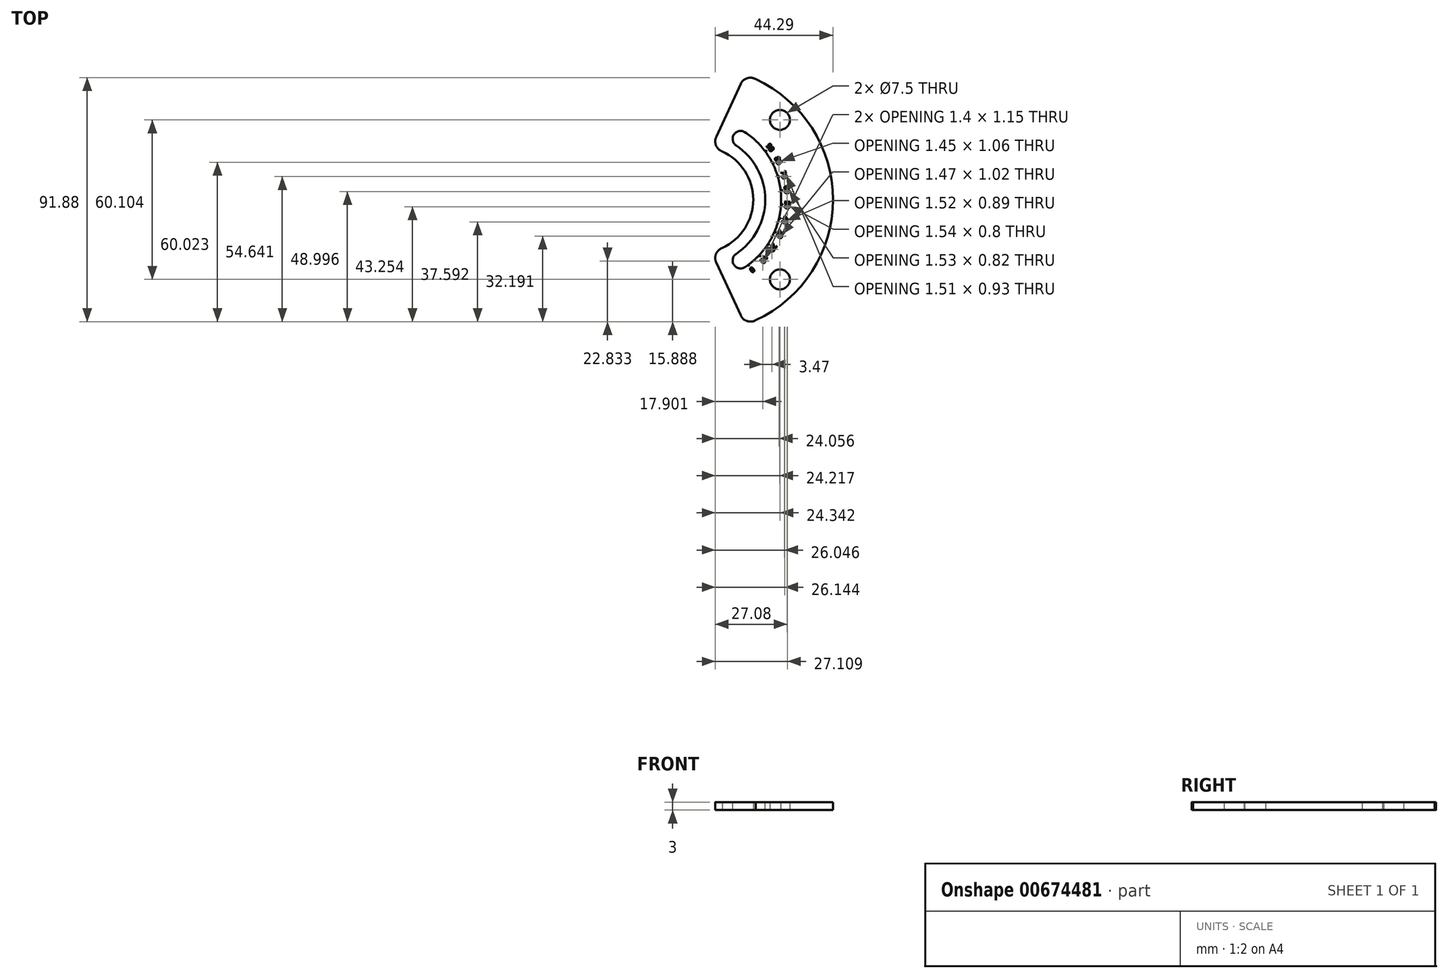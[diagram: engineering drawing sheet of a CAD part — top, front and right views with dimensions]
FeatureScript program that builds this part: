
annotation { "Feature Type Name" : "Feature", "Feature Type Description" : "" }
export const myFeature = defineFeature(function(context is Context, id is Id, definition is map)
    precondition{}
    {
        {
            var Q0;
            Q0=qCreatedBy(makeId("Top.planeOp"),FACE);
            var sketch = newSketch(context, id + "F0", { "sketchPlane" : qUnion([Q0])});
            skCircle(sketch, "E0", {"center": v(0, 0) * mm, "radius": 42.5 * mm, "construction": true});
            skLineSegment(sketch, "E1", {"start": v(0, 0) * mm, "end": v(30.05, 30.05) * mm, "construction": true});
            skCircle(sketch, "E2", {"center": v(30.05, 30.05) * mm, "radius": 3.75 * mm});
            skCircle(sketch, "E3.1.0", {"center": v(-30.05, 30.05) * mm, "radius": 3.75 * mm});
            skCircle(sketch, "E3.2.0", {"center": v(-30.05, -30.05) * mm, "radius": 3.75 * mm});
            skCircle(sketch, "E3.3.0", {"center": v(30.05, -30.05) * mm, "radius": 3.75 * mm});
            skLineSegment(sketch, "E4", {"start": v(0, 0) * mm, "end": v(30.05, -30.05) * mm, "construction": true});
            skSolve(sketch);
        }
        {
            var Q0;
            Q0=qCreatedBy(makeId("Top.planeOp"),FACE);
            var sketch = newSketch(context, id + "F1", { "sketchPlane" : qUnion([Q0])});
            skLineSegment(sketch, "E5", {"start": v(6.08, 23.6) * mm, "end": v(15.3, 43.61) * mm});
            skLineSegment(sketch, "E6", {"start": v(6.08, -23.6) * mm, "end": v(15.3, -43.61) * mm});
            skLineSegment(sketch, "E7", {"start": v(0, 0) * mm, "end": v(0, 47.02) * mm, "construction": true});
            skLineSegment(sketch, "E8", {"start": v(0, 0) * mm, "end": v(0, -46.33) * mm, "construction": true});
            skPoint(sketch, "E9.visualSharp", {"position": v(16.58, 46.4) * mm});
            skArc(sketch, "E9.filletArc", {"start": v(20.9, 45.42) * mm, "mid": v(17.7, 45.75) * mm, "end": v(15.3, 43.61) * mm});
            skPoint(sketch, "E10.visualSharp", {"position": v(3.88, 18.83) * mm});
            skArc(sketch, "E10.filletArc", {"start": v(6.08, 23.6) * mm, "mid": v(6.02, 20.4) * mm, "end": v(8.35, 18.17) * mm});
            skPoint(sketch, "E11.visualSharp", {"position": v(3.88, -18.83) * mm});
            skArc(sketch, "E11.filletArc", {"start": v(8.35, -18.17) * mm, "mid": v(6.02, -20.4) * mm, "end": v(6.08, -23.6) * mm});
            skPoint(sketch, "E12.visualSharp", {"position": v(16.58, -46.4) * mm});
            skArc(sketch, "E12.filletArc", {"start": v(15.3, -43.61) * mm, "mid": v(17.7, -45.75) * mm, "end": v(20.9, -45.42) * mm});
            skLineSegment(sketch, "E13", {"start": v(0, 0) * mm, "end": v(50, 0) * mm, "construction": true});
            skArc(sketch, "E14", {"start": v(8.35, 18.17) * mm, "mid": v(20, 0) * mm, "end": v(8.35, -18.17) * mm});
            skArc(sketch, "E15", {"start": v(20.9, 45.42) * mm, "mid": v(50, 0) * mm, "end": v(20.9, -45.42) * mm});
            skLineSegment(sketch, "E16", {"start": v(20.9, 45.42) * mm, "end": v(20.9, 0) * mm, "construction": true});
            skLineSegment(sketch, "E17", {"start": v(20.9, 0) * mm, "end": v(20.9, -45.42) * mm, "construction": true});
            skLineSegment(sketch, "E18", {"start": v(0, 43.61) * mm, "end": v(15.3, 43.61) * mm, "construction": true});
            skLineSegment(sketch, "E19", {"start": v(0, -43.61) * mm, "end": v(15.3, -43.61) * mm, "construction": true});
            skSolve(sketch);
        }
        {
            var Q0;
            Q0=makeQuery(id+"F1.imprint","IMPRINT",FACE,{"disambiguationData":[TD([[makeQuery(id+"F1.imprint","IMPRINT",EDGE,{"derivedFrom":sQuery(id+"F1.wireOp",EDGE,"E5")}),-1.0]])]});
            extrude(context, id + "F2", {"entities" : qUnion([Q0]), "depth" : 3 * mm, "offsetDistance" : 25 * mm});
        }
        {
            var Q0;
            Q0=makeQuery(id+"F0.imprint","IMPRINT",FACE,{"disambiguationData":[TD([[makeQuery(id+"F0.imprint","IMPRINT",EDGE,{"derivedFrom":sQuery(id+"F0.wireOp",EDGE,"E2")}),1.0]])]});
            var Q1;
            Q1=makeQuery(id+"F0.imprint","IMPRINT",FACE,{"disambiguationData":[TD([[makeQuery(id+"F0.imprint","IMPRINT",EDGE,{"derivedFrom":sQuery(id+"F0.wireOp",EDGE,"E3.3.0")}),1.0]])]});
            extrude(context, id + "F3", {"entities" : qUnion([Q0, Q1]), "operationType" : NewBodyOperationType.REMOVE, "depth" : 25 * mm, "offsetDistance" : 25 * mm});
        }
        {
            var Q0;
            Q0=makeQuery(id+"F2.opExtrude","CAP_FACE",FACE,{"disambiguationData":[OSD([sQuery(id+"F1.wireOp",EDGE,"KiuFZQME-wWnU-ktu5-Gd9x-qji5TMNZz2fd"),sQuery(id+"F1.wireOp",EDGE,"G5eraXv0-ftC7-V2Hx-4i3N-1R2XA50WnSdq"),sQuery(id+"F1.wireOp",EDGE,"E5"),sQuery(id+"F1.wireOp",EDGE,"E6"),sQuery(id+"F1.wireOp",EDGE,"57560024-62e8-479f-91f4-8b403f4d0ad7.filletArc"),sQuery(id+"F1.wireOp",EDGE,"ddf71622-e854-4fa8-aca5-087326283111.filletArc"),sQuery(id+"F1.wireOp",EDGE,"85b82a5b-4425-4996-801d-5779b438c59f.filletArc"),sQuery(id+"F1.wireOp",EDGE,"35c327b1-5974-4460-b54d-dc77ba413df5.filletArc")])],"isStart":false});
            var sketch = newSketch(context, id + "F4", { "sketchPlane" : qUnion([Q0])});
            skArc(sketch, "E20", {"start": v(13.6, 20.4) * mm, "mid": v(24.52, 0) * mm, "end": v(13.6, -20.4) * mm});
            skArc(sketch, "E21", {"start": v(16.92, 25.4) * mm, "mid": v(30.52, 0) * mm, "end": v(16.92, -25.4) * mm});
            skLineSegment(sketch, "E22", {"start": v(0, 0) * mm, "end": v(16.92, -25.4) * mm, "construction": true});
            skLineSegment(sketch, "E23", {"start": v(0, 0) * mm, "end": v(16.92, 25.4) * mm, "construction": true});
            skLineSegment(sketch, "E24", {"start": v(13.6, 20.4) * mm, "end": v(13.6, 0) * mm, "construction": true});
            skLineSegment(sketch, "E25", {"start": v(13.6, 0) * mm, "end": v(13.6, -20.4) * mm, "construction": true});
            skArc(sketch, "E26", {"start": v(13.6, 20.4) * mm, "mid": v(12.76, 24.57) * mm, "end": v(16.92, 25.4) * mm});
            skArc(sketch, "E27", {"start": v(13.6, -20.4) * mm, "mid": v(12.76, -24.57) * mm, "end": v(16.92, -25.4) * mm});
            skSolve(sketch);
        }
        {
            var Q0;
            Q0=qSketchRegion(id+"F4",true);
            extrude(context, id + "F5", {"entities" : qUnion([Q0]), "operationType" : NewBodyOperationType.REMOVE, "oppositeDirection" : true, "depth" : 25 * mm, "offsetDistance" : 25 * mm});
        }
        {
            var Q0;
            Q0=makeQuery(id+"F2.opExtrude","CAP_FACE",FACE,{"disambiguationData":[OSD([sQuery(id+"F1.wireOp",EDGE,"E5"),sQuery(id+"F1.wireOp",EDGE,"E6"),sQuery(id+"F1.wireOp",EDGE,"E9.filletArc"),sQuery(id+"F1.wireOp",EDGE,"E10.filletArc"),sQuery(id+"F1.wireOp",EDGE,"E11.filletArc"),sQuery(id+"F1.wireOp",EDGE,"E12.filletArc"),sQuery(id+"F1.wireOp",EDGE,"E14"),sQuery(id+"F1.wireOp",EDGE,"E15")])],"isStart":false});
            var sketch = newSketch(context, id + "F6", { "sketchPlane" : qUnion([Q0])});
            skLineSegment(sketch, "E28", {"start": v(0, 39.25) * mm, "end": v(0, -36.96) * mm, "construction": true});
            skPoint(sketch, "E29.center", {"position": v(0, 0) * mm});
            skLineSegment(sketch, "E30.1.0", {"start": v(21.84, -20.36) * mm, "end": v(21.67, -20.54) * mm});
            skLineSegment(sketch, "E30.1.1", {"start": v(22.8, -21.26) * mm, "end": v(21.84, -20.36) * mm});
            skLineSegment(sketch, "E30.1.2", {"start": v(21.67, -20.54) * mm, "end": v(22.63, -21.44) * mm});
            skLineSegment(sketch, "E30.1.3", {"start": v(22.63, -21.44) * mm, "end": v(22.8, -21.26) * mm});
            skLineSegment(sketch, "E30.2.0", {"start": v(25.04, -16.27) * mm, "end": v(24.9, -16.48) * mm});
            skLineSegment(sketch, "E30.2.1", {"start": v(26.14, -16.99) * mm, "end": v(25.04, -16.27) * mm});
            skLineSegment(sketch, "E30.2.2", {"start": v(24.9, -16.48) * mm, "end": v(26, -17.2) * mm});
            skLineSegment(sketch, "E30.2.3", {"start": v(26, -17.2) * mm, "end": v(26.14, -16.99) * mm});
            skLineSegment(sketch, "E30.3.0", {"start": v(27.48, -11.68) * mm, "end": v(27.38, -11.91) * mm});
            skLineSegment(sketch, "E30.3.1", {"start": v(28.69, -12.2) * mm, "end": v(27.48, -11.68) * mm});
            skLineSegment(sketch, "E30.3.2", {"start": v(27.38, -11.91) * mm, "end": v(28.59, -12.43) * mm});
            skLineSegment(sketch, "E30.3.3", {"start": v(28.59, -12.43) * mm, "end": v(28.69, -12.2) * mm});
            skLineSegment(sketch, "E30.4.0", {"start": v(29.09, -6.75) * mm, "end": v(29.03, -7) * mm});
            skLineSegment(sketch, "E30.4.1", {"start": v(30.37, -7.05) * mm, "end": v(29.09, -6.75) * mm});
            skLineSegment(sketch, "E30.4.2", {"start": v(29.03, -7) * mm, "end": v(30.31, -7.3) * mm});
            skLineSegment(sketch, "E30.4.3", {"start": v(30.31, -7.3) * mm, "end": v(30.37, -7.05) * mm});
            skLineSegment(sketch, "E30.5.0", {"start": v(29.81, -1.6) * mm, "end": v(29.8, -1.86) * mm});
            skLineSegment(sketch, "E30.5.1", {"start": v(31.13, -1.69) * mm, "end": v(29.81, -1.6) * mm});
            skLineSegment(sketch, "E30.5.2", {"start": v(29.8, -1.86) * mm, "end": v(31.12, -1.94) * mm});
            skLineSegment(sketch, "E30.5.3", {"start": v(31.12, -1.94) * mm, "end": v(31.13, -1.69) * mm});
            skLineSegment(sketch, "E30.6.0", {"start": v(29.64, 3.58) * mm, "end": v(29.67, 3.33) * mm});
            skLineSegment(sketch, "E30.6.1", {"start": v(30.95, 3.73) * mm, "end": v(29.64, 3.58) * mm});
            skLineSegment(sketch, "E30.6.2", {"start": v(29.67, 3.33) * mm, "end": v(30.98, 3.48) * mm});
            skLineSegment(sketch, "E30.6.3", {"start": v(30.98, 3.48) * mm, "end": v(30.95, 3.73) * mm});
            skLineSegment(sketch, "E30.7.0", {"start": v(28.58, 8.66) * mm, "end": v(28.65, 8.42) * mm});
            skLineSegment(sketch, "E30.7.1", {"start": v(29.84, 9.04) * mm, "end": v(28.58, 8.66) * mm});
            skLineSegment(sketch, "E30.7.2", {"start": v(28.65, 8.42) * mm, "end": v(29.9, 8.8) * mm});
            skLineSegment(sketch, "E30.7.3", {"start": v(29.9, 8.8) * mm, "end": v(29.84, 9.04) * mm});
            skLineSegment(sketch, "E30.8.0", {"start": v(26.64, 13.48) * mm, "end": v(26.76, 13.25) * mm});
            skLineSegment(sketch, "E30.8.1", {"start": v(27.82, 14.07) * mm, "end": v(26.64, 13.48) * mm});
            skLineSegment(sketch, "E30.8.2", {"start": v(26.76, 13.25) * mm, "end": v(27.93, 13.84) * mm});
            skLineSegment(sketch, "E30.8.3", {"start": v(27.93, 13.84) * mm, "end": v(27.82, 14.07) * mm});
            skLineSegment(sketch, "E30.anchor1", {"start": v(0, 0) * mm, "end": v(17.79, -23.98) * mm, "construction": true});
            skLineSegment(sketch, "E31.2.9.0", {"start": v(23.9, 17.89) * mm, "end": v(24.06, 17.69) * mm});
            skLineSegment(sketch, "E31.3.9.0", {"start": v(24.97, 18.67) * mm, "end": v(23.9, 17.89) * mm});
            skLineSegment(sketch, "E31.6.9.0", {"start": v(24.06, 17.69) * mm, "end": v(25.11, 18.47) * mm});
            skLineSegment(sketch, "E31.9.9.0", {"start": v(25.11, 18.47) * mm, "end": v(24.97, 18.67) * mm});
            skLineSegment(sketch, "E32", {"start": v(0, 0) * mm, "end": v(24.51, 18.18) * mm, "construction": true});
            skLineSegment(sketch, "E33", {"start": v(17.79, -23.98) * mm, "end": v(17.69, -24.06) * mm});
            skLineSegment(sketch, "E34", {"start": v(17.69, -24.06) * mm, "end": v(18.38, -24.99) * mm});
            skLineSegment(sketch, "E35", {"start": v(18.38, -24.99) * mm, "end": v(18.58, -24.84) * mm});
            skLineSegment(sketch, "E36", {"start": v(18.58, -24.84) * mm, "end": v(17.89, -23.9) * mm});
            skLineSegment(sketch, "E37", {"start": v(17.89, -23.9) * mm, "end": v(17.79, -23.98) * mm});
            skLineSegment(sketch, "E38.1.0", {"start": v(0, 0) * mm, "end": v(21.68, -20.53) * mm, "construction": true});
            skLineSegment(sketch, "E38.2.0", {"start": v(0, 0) * mm, "end": v(24.92, -16.45) * mm, "construction": true});
            skLineSegment(sketch, "E38.3.0", {"start": v(0, 0) * mm, "end": v(27.4, -11.88) * mm, "construction": true});
            skLineSegment(sketch, "E38.4.0", {"start": v(0, 0) * mm, "end": v(29.04, -6.94) * mm, "construction": true});
            skLineSegment(sketch, "E38.5.0", {"start": v(0, 0) * mm, "end": v(29.8, -1.8) * mm, "construction": true});
            skLineSegment(sketch, "E38.6.0", {"start": v(0, 0) * mm, "end": v(29.66, 3.41) * mm, "construction": true});
            skLineSegment(sketch, "E38.7.0", {"start": v(0, 0) * mm, "end": v(28.62, 8.51) * mm, "construction": true});
            skLineSegment(sketch, "E38.8.0", {"start": v(0, 0) * mm, "end": v(26.7, 13.35) * mm, "construction": true});
            skLineSegment(sketch, "E38.9.0", {"start": v(0, 0) * mm, "end": v(23.98, 17.79) * mm, "construction": true});
            skLineSegment(sketch, "E38.anchor2", {"start": v(0, 0) * mm, "end": v(23.98, 17.79) * mm, "construction": true});
            skSolve(sketch);
        }
        {
            var Q0;
            {var subQ0=sQuery(id+"F6.wireOp",EDGE,"594Twtlv-L5ni-ZomQ-KuFa-bSSoLLlrFaCu");Q0=makeQuery(id+"F6.imprint","IMPRINT",FACE,{"disambiguationData":[TD([[makeQuery(id+"F6.imprint","IMPRINT",EDGE,{"derivedFrom":subQ0}),1.0]])]});}
            var Q1;
            {var subQ0=sQuery(id+"F6.wireOp",EDGE,"YlrvQvtq-lzJw-h0mC-7lxV-1P0NOcUl3Lp0");Q1=makeQuery(id+"F6.imprint","IMPRINT",FACE,{"disambiguationData":[TD([[makeQuery(id+"F6.imprint","IMPRINT",EDGE,{"derivedFrom":subQ0}),1.0]])]});}
            var Q2;
            {var subQ0=sQuery(id+"F6.wireOp",EDGE,"E30.1.0");Q2=makeQuery(id+"F6.imprint","IMPRINT",FACE,{"disambiguationData":[TD([[makeQuery(id+"F6.imprint","IMPRINT",EDGE,{"derivedFrom":subQ0}),1.0]])]});}
            var Q3;
            {var subQ0=sQuery(id+"F6.wireOp",EDGE,"E30.1.3");Q3=makeQuery(id+"F6.imprint","IMPRINT",FACE,{"disambiguationData":[TD([[makeQuery(id+"F6.imprint","IMPRINT",EDGE,{"derivedFrom":subQ0}),1.0]])]});}
            var Q4;
            {var subQ0=sQuery(id+"F6.wireOp",EDGE,"E30.2.0");Q4=makeQuery(id+"F6.imprint","IMPRINT",FACE,{"disambiguationData":[TD([[makeQuery(id+"F6.imprint","IMPRINT",EDGE,{"derivedFrom":subQ0}),1.0]])]});}
            var Q5;
            {var subQ0=sQuery(id+"F6.wireOp",EDGE,"E30.2.3");Q5=makeQuery(id+"F6.imprint","IMPRINT",FACE,{"disambiguationData":[TD([[makeQuery(id+"F6.imprint","IMPRINT",EDGE,{"derivedFrom":subQ0}),1.0]])]});}
            var Q6;
            {var subQ0=sQuery(id+"F6.wireOp",EDGE,"E30.3.0");Q6=makeQuery(id+"F6.imprint","IMPRINT",FACE,{"disambiguationData":[TD([[makeQuery(id+"F6.imprint","IMPRINT",EDGE,{"derivedFrom":subQ0}),1.0]])]});}
            var Q7;
            {var subQ0=sQuery(id+"F6.wireOp",EDGE,"E30.3.3");Q7=makeQuery(id+"F6.imprint","IMPRINT",FACE,{"disambiguationData":[TD([[makeQuery(id+"F6.imprint","IMPRINT",EDGE,{"derivedFrom":subQ0}),1.0]])]});}
            var Q8;
            {var subQ0=sQuery(id+"F6.wireOp",EDGE,"E30.4.0");Q8=makeQuery(id+"F6.imprint","IMPRINT",FACE,{"disambiguationData":[TD([[makeQuery(id+"F6.imprint","IMPRINT",EDGE,{"derivedFrom":subQ0}),1.0]])]});}
            var Q9;
            {var subQ0=sQuery(id+"F6.wireOp",EDGE,"E30.4.3");Q9=makeQuery(id+"F6.imprint","IMPRINT",FACE,{"disambiguationData":[TD([[makeQuery(id+"F6.imprint","IMPRINT",EDGE,{"derivedFrom":subQ0}),1.0]])]});}
            var Q10;
            {var subQ0=sQuery(id+"F6.wireOp",EDGE,"E30.5.0");Q10=makeQuery(id+"F6.imprint","IMPRINT",FACE,{"disambiguationData":[TD([[makeQuery(id+"F6.imprint","IMPRINT",EDGE,{"derivedFrom":subQ0}),1.0]])]});}
            var Q11;
            {var subQ0=sQuery(id+"F6.wireOp",EDGE,"E30.6.0");Q11=makeQuery(id+"F6.imprint","IMPRINT",FACE,{"disambiguationData":[TD([[makeQuery(id+"F6.imprint","IMPRINT",EDGE,{"derivedFrom":subQ0}),1.0]])]});}
            var Q12;
            {var subQ0=sQuery(id+"F6.wireOp",EDGE,"E30.6.3");Q12=makeQuery(id+"F6.imprint","IMPRINT",FACE,{"disambiguationData":[TD([[makeQuery(id+"F6.imprint","IMPRINT",EDGE,{"derivedFrom":subQ0}),1.0]])]});}
            var Q13;
            {var subQ0=sQuery(id+"F6.wireOp",EDGE,"E30.5.3");Q13=makeQuery(id+"F6.imprint","IMPRINT",FACE,{"disambiguationData":[TD([[makeQuery(id+"F6.imprint","IMPRINT",EDGE,{"derivedFrom":subQ0}),1.0]])]});}
            var Q14;
            {var subQ0=sQuery(id+"F6.wireOp",EDGE,"E30.7.0");Q14=makeQuery(id+"F6.imprint","IMPRINT",FACE,{"disambiguationData":[TD([[makeQuery(id+"F6.imprint","IMPRINT",EDGE,{"derivedFrom":subQ0}),1.0]])]});}
            var Q15;
            {var subQ0=sQuery(id+"F6.wireOp",EDGE,"E30.7.3");Q15=makeQuery(id+"F6.imprint","IMPRINT",FACE,{"disambiguationData":[TD([[makeQuery(id+"F6.imprint","IMPRINT",EDGE,{"derivedFrom":subQ0}),1.0]])]});}
            var Q16;
            {var subQ0=sQuery(id+"F6.wireOp",EDGE,"E30.8.0");Q16=makeQuery(id+"F6.imprint","IMPRINT",FACE,{"disambiguationData":[TD([[makeQuery(id+"F6.imprint","IMPRINT",EDGE,{"derivedFrom":subQ0}),1.0]])]});}
            var Q17;
            {var subQ0=sQuery(id+"F6.wireOp",EDGE,"E30.8.3");Q17=makeQuery(id+"F6.imprint","IMPRINT",FACE,{"disambiguationData":[TD([[makeQuery(id+"F6.imprint","IMPRINT",EDGE,{"derivedFrom":subQ0}),1.0]])]});}
            var Q18;
            {var subQ0=sQuery(id+"F6.wireOp",EDGE,"E35");Q18=makeQuery(id+"F6.imprint","IMPRINT",FACE,{"disambiguationData":[TD([[makeQuery(id+"F6.imprint","IMPRINT",EDGE,{"derivedFrom":subQ0}),1.0]])]});}
            var Q19;
            {var subQ2=sQuery(id+"F6.wireOp",EDGE,"E33");Q19=makeQuery(id+"F6.imprint","IMPRINT",FACE,{"disambiguationData":[TD([[makeQuery(id+"F6.imprint","IMPRINT",EDGE,{"derivedFrom":subQ2}),1.0]])]});}
            var Q20;
            {var subQ0=sQuery(id+"F6.wireOp",EDGE,"E31.9.9.0");Q20=makeQuery(id+"F6.imprint","IMPRINT",FACE,{"disambiguationData":[TD([[makeQuery(id+"F6.imprint","IMPRINT",EDGE,{"derivedFrom":subQ0}),1.0]])]});}
            var Q21;
            {var subQ0=sQuery(id+"F6.wireOp",EDGE,"E31.2.9.0");Q21=makeQuery(id+"F6.imprint","IMPRINT",FACE,{"disambiguationData":[TD([[makeQuery(id+"F6.imprint","IMPRINT",EDGE,{"derivedFrom":subQ0}),1.0]])]});}
            extrude(context, id + "F7", {"entities" : qUnion([Q0, Q1, Q2, Q3, Q4, Q5, Q6, Q7, Q8, Q9, Q10, Q11, Q12, Q13, Q14, Q15, Q16, Q17, Q18, Q19, Q20, Q21]), "operationType" : NewBodyOperationType.REMOVE, "oppositeDirection" : true, "depth" : 0.1 * mm, "offsetDistance" : 25 * mm});
        }
        {
            var Q0;
            Q0=makeQuery(id+"F2.opExtrude","CAP_FACE",FACE,{"disambiguationData":[OSD([sQuery(id+"F1.wireOp",EDGE,"E5"),sQuery(id+"F1.wireOp",EDGE,"E6"),sQuery(id+"F1.wireOp",EDGE,"E9.filletArc"),sQuery(id+"F1.wireOp",EDGE,"E10.filletArc"),sQuery(id+"F1.wireOp",EDGE,"E11.filletArc"),sQuery(id+"F1.wireOp",EDGE,"E12.filletArc"),sQuery(id+"F1.wireOp",EDGE,"E14"),sQuery(id+"F1.wireOp",EDGE,"E15")])],"isStart":false});
            var sketch = newSketch(context, id + "F8", { "sketchPlane" : qUnion([Q0])});
            skText(sketch, "E39", { "text": "10", "fontName": "OpenSans-Regular.ttf"});
            skText(sketch, "E40", { "text": "20", "fontName": "OpenSans-Regular.ttf"});
            skPoint(sketch, "E41", {"position": v(26.88, -14.45) * mm});
            skText(sketch, "E42", { "text": "30", "fontName": "OpenSans-Regular.ttf"});
            skText(sketch, "E43", { "text": "40\n", "fontName": "OpenSans-Regular.ttf"});
            skText(sketch, "E44", { "text": "50", "fontName": "OpenSans-Regular.ttf"});
            skText(sketch, "E45", { "text": "60", "fontName": "OpenSans-Regular.ttf"});
            skText(sketch, "E46", { "text": "70", "fontName": "OpenSans-Regular.ttf"});
            skText(sketch, "E47", { "text": "80", "fontName": "OpenSans-Regular.ttf"});
            skText(sketch, "E48", { "text": "90", "fontName": "OpenSans-Regular.ttf"});
            skText(sketch, "E49", { "text": "0", "fontName": "OpenSans-Regular.ttf"});
            skLineSegment(sketch, "E50", {"start": v(0, 0) * mm, "end": v(19.06, -25.7) * mm, "construction": true});
            skLineSegment(sketch, "E51", {"start": v(0, 0) * mm, "end": v(23.24, -22) * mm, "construction": true});
            skLineSegment(sketch, "E52", {"start": v(0, 0) * mm, "end": v(26.7, -17.63) * mm, "construction": true});
            skLineSegment(sketch, "E53", {"start": v(0, 0) * mm, "end": v(29.36, -12.73) * mm, "construction": true});
            skLineSegment(sketch, "E54", {"start": v(0, 0) * mm, "end": v(31.12, -7.44) * mm, "construction": true});
            skLineSegment(sketch, "E55", {"start": v(0, 0) * mm, "end": v(31.94, -1.92) * mm, "construction": true});
            skLineSegment(sketch, "E56", {"start": v(0, 0) * mm, "end": v(31.8, 3.66) * mm, "construction": true});
            skPoint(sketch, "E56.endSnap0", {"position": v(31.8, 3.66) * mm});
            skLineSegment(sketch, "E57", {"start": v(0, 0) * mm, "end": v(30.67, 9.12) * mm, "construction": true});
            skLineSegment(sketch, "E58", {"start": v(0, 0) * mm, "end": v(28.62, 14.3) * mm, "construction": true});
            skLineSegment(sketch, "E59", {"start": v(0, 0) * mm, "end": v(25.7, 19.06) * mm, "construction": true});
            const initialGuessF8  = {"E39": [0.02406, -0.02075, -0.55104, -0.83448, 0.00186], "E40": [0.02753, -0.01638, -0.55104, -0.83448, 0.00186], "E42": [0.02996, -0.01135, -0.39776, -0.91749, 0.00186], "E43": [0.03147, -0.00598, -0.2324, -0.97262, 0.00186], "E44": [0.03203, -0.00042, -0.05998, -0.9982, 0.00186], "E45": [0.03162, 0.00515, 0.11427, -0.99345, 0.00186], "E46": [0.03024, 0.01056, 0.28505, -0.95851, 0.00186], "E47": [0.02795, 0.01565, 0.44716, -0.89445, 0.00186], "E48": [0.0248, 0.02027, 0.59569, -0.80322, 0.00186], "E49": [0.01966, -0.02526, -0.80322, -0.59569, 0.00184]};
            skSetInitialGuess(sketch, initialGuessF8);
            skSolve(sketch);
        }
        {
            var Q0;
            Q0 = qSketchRegion(id + "F8", true);
            extrude(context, id + "F9", {"entities" : qUnion([Q0]), "operationType" : NewBodyOperationType.REMOVE, "oppositeDirection" : true, "depth" : 0.1 * mm, "offsetDistance" : 25 * mm});
        }
        {
            var Q0;
            Q0 = qSketchRegion(id + "F8", true);
            extrude(context, id + "F10", {"entities" : qUnion([Q0]), "oppositeDirection" : true, "depth" : 0.1 * mm, "offsetDistance" : 25 * mm});
        }
    });
